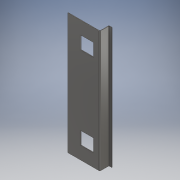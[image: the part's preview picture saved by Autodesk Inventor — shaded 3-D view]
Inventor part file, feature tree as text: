
AUTODESK INVENTOR PART (.ipt)
format: ipt  version: 2017 (Build 210142000, 142)  size: 176,640 bytes
history: native  units: mm
features: sheet_metal_op x6, sketch x3, other x3, extrude x1
ambient origin geometry x8: Origin, YZ Plane, XZ Plane, XY Plane, X Axis, Y Axis, Z Axis, Center Point
bodies: Solid1 (feature_tree)
feature tree (13):
  sheet_metal_op  "Contour Flange1"
  sheet_metal_op  "Flange1"
  extrude  "Extrusion1"  Depth=30.0mm
  sketch  "Sketch1"  dims[d0=100.0mm d1=30.0mm]
  other  "Plate1"
  sheet_metal_op  "Bend1"
  sheet_metal_op  "Corner1"
  sketch  "Sketch2"  dims[d2=1.5mm]
  other  "Plate2"
  sheet_metal_op  "Bend2"
  sheet_metal_op  "Corner2"
  sketch  "Sketch3"  dims[d3=0.75mm d4=3.0mm d5=1.5mm d6=378.5mm d7=1.5mm d8=0.5mm d9=6.0mm d10=1.5mm d11=1.5mm d12=1.5mm d13=0.75mm d14=3.0mm d15=1.5mm d16=10.0mm d17=90.0deg d18=1.5mm d19=6.0mm d20=1.5mm d21=1.5mm d24=40.0mm d25=40.0mm d26=60.0mm d27=60.0mm d28=40.0mm d29=40.0mm d30=60.0mm d31=60.0mm d32=1.5mm d33=0.0mm]
  other  "Definition1"
